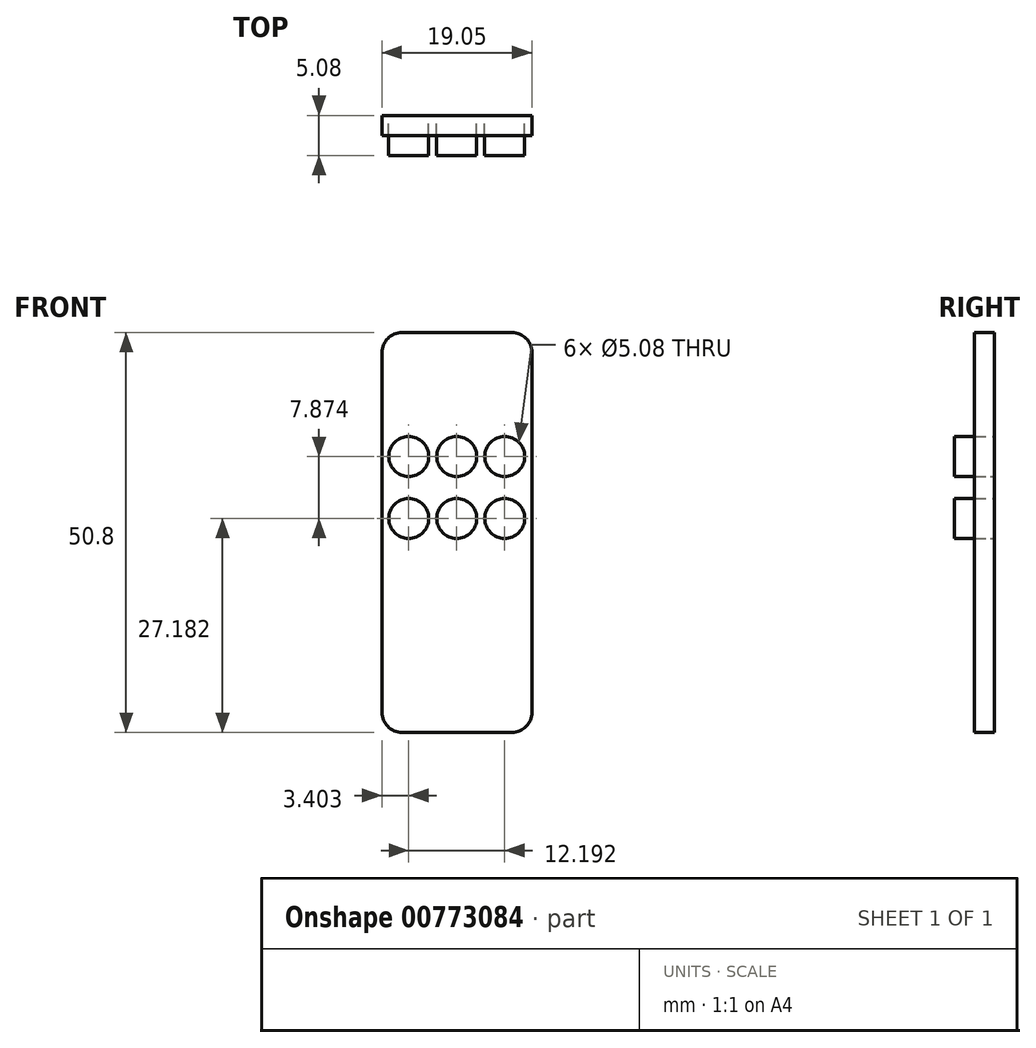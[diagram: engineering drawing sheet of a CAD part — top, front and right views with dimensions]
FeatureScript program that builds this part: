
annotation { "Feature Type Name" : "Feature", "Feature Type Description" : "" }
export const myFeature = defineFeature(function(context is Context, id is Id, definition is map)
    precondition{}
    {
        {
            var Q0;
            Q0=qCreatedBy(makeId("Front.planeOp"),FACE);
            var sketch = newSketch(context, id + "F0", { "sketchPlane" : qUnion([Q0])});
            skLineSegment(sketch, "E0.bottom", {"start": v(2.54, 25.4) * mm, "end": v(16.51, 25.4) * mm});
            skLineSegment(sketch, "E0.top", {"start": v(2.54, -25.4) * mm, "end": v(16.51, -25.4) * mm});
            skLineSegment(sketch, "E0.left", {"start": v(0, 22.86) * mm, "end": v(0, -22.86) * mm});
            skLineSegment(sketch, "E0.right", {"start": v(19.05, 22.86) * mm, "end": v(19.05, -22.86) * mm});
            skPoint(sketch, "E1.visualSharp", {"position": v(0, 25.4) * mm});
            skArc(sketch, "E1.filletArc", {"start": v(2.54, 25.4) * mm, "mid": v(0.74, 24.66) * mm, "end": v(0, 22.86) * mm});
            skPoint(sketch, "E2.visualSharp", {"position": v(19.05, 25.4) * mm});
            skArc(sketch, "E2.filletArc", {"start": v(19.05, 22.86) * mm, "mid": v(18.3, 24.66) * mm, "end": v(16.51, 25.4) * mm});
            skPoint(sketch, "E3.visualSharp", {"position": v(19.05, -25.4) * mm});
            skArc(sketch, "E3.filletArc", {"start": v(16.51, -25.4) * mm, "mid": v(18.3, -24.66) * mm, "end": v(19.05, -22.86) * mm});
            skPoint(sketch, "E4.visualSharp", {"position": v(0, -25.4) * mm});
            skArc(sketch, "E4.filletArc", {"start": v(0, -22.86) * mm, "mid": v(0.74, -24.66) * mm, "end": v(2.54, -25.4) * mm});
            skCircle(sketch, "E5", {"center": v(3.4, 9.66) * mm, "radius": 2.54 * mm});
            skCircle(sketch, "E6.0.1.0", {"center": v(3.4, 1.78) * mm, "radius": 2.54 * mm});
            skCircle(sketch, "E6.1.0.0", {"center": v(9.5, 9.66) * mm, "radius": 2.54 * mm});
            skCircle(sketch, "E6.1.1.0", {"center": v(9.5, 1.78) * mm, "radius": 2.54 * mm});
            skCircle(sketch, "E6.2.0.0", {"center": v(15.6, 9.66) * mm, "radius": 2.54 * mm});
            skCircle(sketch, "E6.2.1.0", {"center": v(15.6, 1.78) * mm, "radius": 2.54 * mm});
            skLineSegment(sketch, "E6.direction1", {"start": v(3.4, 9.66) * mm, "end": v(9.5, 9.66) * mm, "construction": true});
            skLineSegment(sketch, "E6.direction2", {"start": v(3.4, 9.66) * mm, "end": v(3.4, 1.78) * mm, "construction": true});
            skSolve(sketch);
        }
        {
            var Q0;
            Q0=makeQuery(id+"F0.imprint","IMPRINT",FACE,{"disambiguationData":[TD([[makeQuery(id+"F0.imprint","IMPRINT",EDGE,{"derivedFrom":sQuery(id+"F0.wireOp",EDGE,"E5")}),1.0]])]});
            var Q1;
            Q1=makeQuery(id+"F0.imprint","IMPRINT",FACE,{"disambiguationData":[TD([[makeQuery(id+"F0.imprint","IMPRINT",EDGE,{"derivedFrom":sQuery(id+"F0.wireOp",EDGE,"E6.1.0.0")}),1.0]])]});
            var Q2;
            Q2=makeQuery(id+"F0.imprint","IMPRINT",FACE,{"disambiguationData":[TD([[makeQuery(id+"F0.imprint","IMPRINT",EDGE,{"derivedFrom":sQuery(id+"F0.wireOp",EDGE,"E6.2.0.0")}),1.0]])]});
            var Q3;
            Q3=makeQuery(id+"F0.imprint","IMPRINT",FACE,{"disambiguationData":[TD([[makeQuery(id+"F0.imprint","IMPRINT",EDGE,{"derivedFrom":sQuery(id+"F0.wireOp",EDGE,"E6.2.1.0")}),1.0]])]});
            var Q4;
            Q4=makeQuery(id+"F0.imprint","IMPRINT",FACE,{"disambiguationData":[TD([[makeQuery(id+"F0.imprint","IMPRINT",EDGE,{"derivedFrom":sQuery(id+"F0.wireOp",EDGE,"E6.1.1.0")}),1.0]])]});
            var Q5;
            Q5=makeQuery(id+"F0.imprint","IMPRINT",FACE,{"disambiguationData":[TD([[makeQuery(id+"F0.imprint","IMPRINT",EDGE,{"derivedFrom":sQuery(id+"F0.wireOp",EDGE,"E6.0.1.0")}),1.0]])]});
            extrude(context, id + "F1", {"entities" : qUnion([Q0, Q1, Q2, Q3, Q4, Q5]), "depth" : 5.08 * mm, "offsetDistance" : 25.4 * mm});
        }
        {
            var Q0;
            Q0 = qSketchRegion(id + "F0", true);
            extrude(context, id + "F2", {"entities" : qUnion([Q0]), "depth" : 2.54 * mm, "offsetDistance" : 25.4 * mm});
        }
    });
